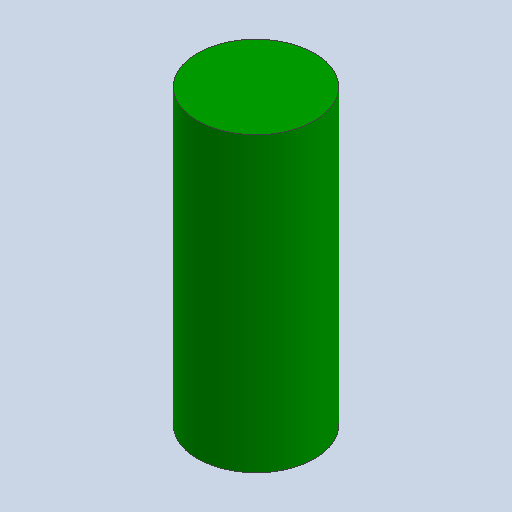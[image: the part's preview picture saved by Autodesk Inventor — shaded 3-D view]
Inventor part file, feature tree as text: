
AUTODESK INVENTOR PART (.ipt)
format: ipt  version: 2025.2 (Build 292293000, 293)  size: 90,112 bytes
history: native  units: in
note: dims shown in document units (in); Inventor stores cm internally (conversion verified against a paired STEP export)
features: other x3, sketch x1
ambient origin geometry x8: Origin, YZ Plane, XZ Plane, XY Plane, X Axis, Y Axis, Z Axis, Center Point
bodies: Solid1 (feature_tree)
feature tree (4):
  other  "26650(Green).ipt"
  other  "Solid1::26650(Green).ipt"
  other  "TaggingFeature1"
  sketch  "Sketch1"  dims[d0=0.3937in]
